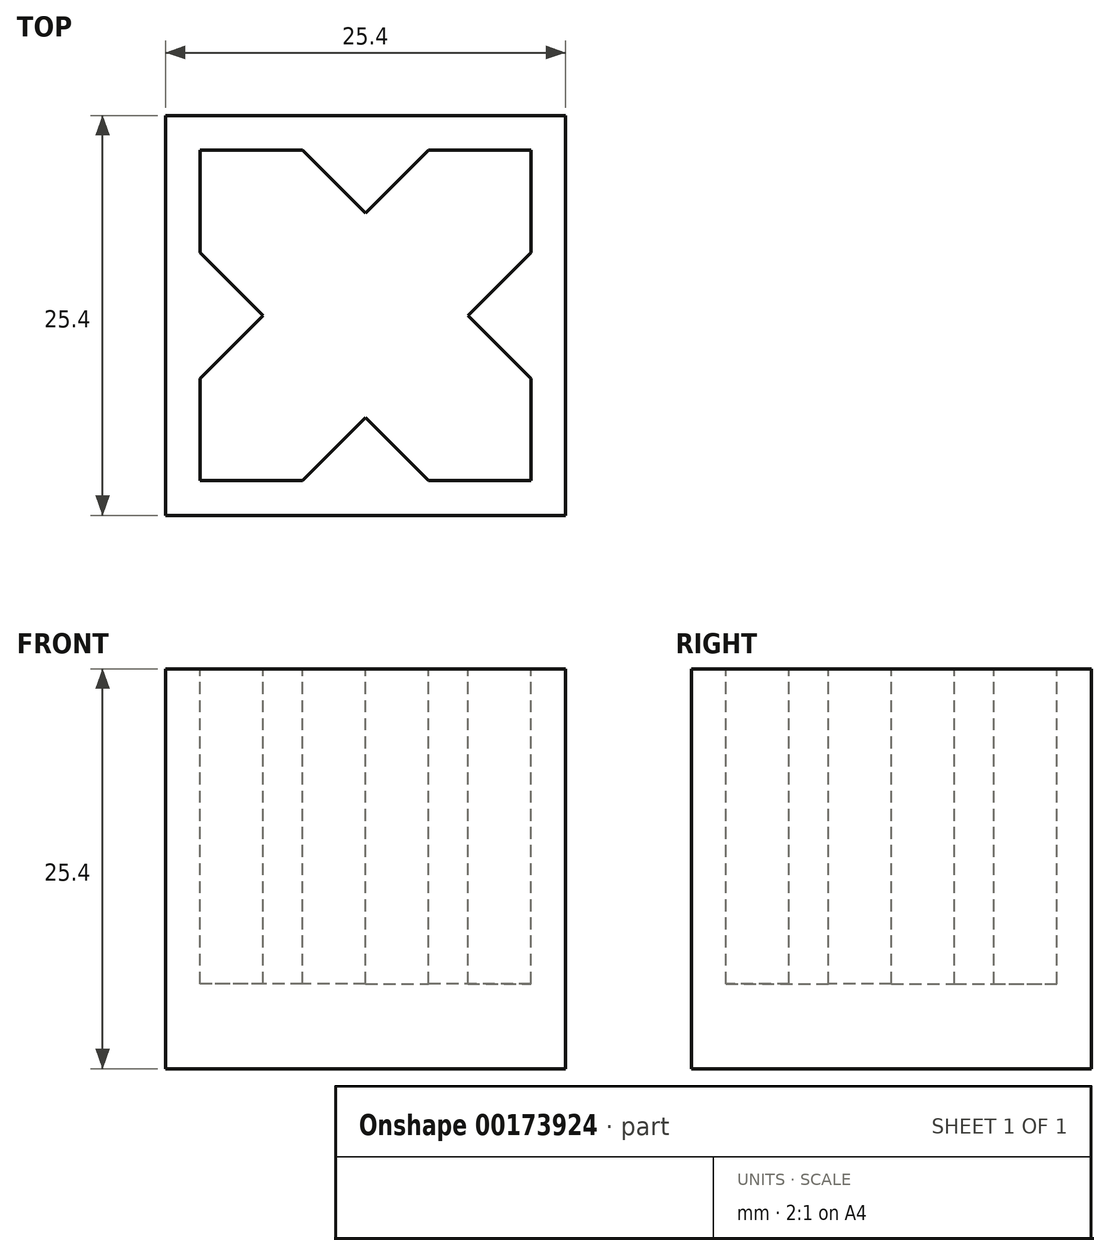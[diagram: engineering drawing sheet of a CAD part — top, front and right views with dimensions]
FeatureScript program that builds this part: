
annotation { "Feature Type Name" : "Feature", "Feature Type Description" : "" }
export const myFeature = defineFeature(function(context is Context, id is Id, definition is map)
    precondition{}
    {
        {
            var Q0;
            Q0=qCreatedBy(makeId("Top.planeOp"),FACE);
            var sketch = newSketch(context, id + "F0", { "sketchPlane" : qUnion([Q0])});
            skLineSegment(sketch, "E0.bottom", {"start": v(0, 0) * mm, "end": v(25.4, 0) * mm});
            skLineSegment(sketch, "E0.top", {"start": v(0, 25.4) * mm, "end": v(25.4, 25.4) * mm});
            skLineSegment(sketch, "E0.left", {"start": v(0, 0) * mm, "end": v(0, 25.4) * mm});
            skLineSegment(sketch, "E0.right", {"start": v(25.4, 0) * mm, "end": v(25.4, 25.4) * mm});
            skSolve(sketch);
        }
        {
            var Q0;
            Q0 = qSketchRegion(id + "F0", true);
            extrude(context, id + "F1", {"entities" : qUnion([Q0]), "depth" : 25.4 * mm});
        }
        {
            var Q0;
            Q0=makeQuery(id+"F1.opExtrude","CAP_FACE",FACE,{"disambiguationData":[OSD([sQuery(id+"F0.wireOp",EDGE,"E0.bottom"),sQuery(id+"F0.wireOp",EDGE,"E0.top"),sQuery(id+"F0.wireOp",EDGE,"E0.left"),sQuery(id+"F0.wireOp",EDGE,"E0.right")])],"isStart":false});
            var sketch = newSketch(context, id + "F2", { "sketchPlane" : qUnion([Q0])});
            skLineSegment(sketch, "E1", {"start": v(0, 12.7) * mm, "end": v(25.4, 12.7) * mm});
            skLineSegment(sketch, "E2", {"start": v(12.7, 25.4) * mm, "end": v(12.7, 0) * mm});
            skLineSegment(sketch, "E3.bottom", {"start": v(23.2, 2.2) * mm, "end": v(2.2, 2.2) * mm});
            skLineSegment(sketch, "E3.top", {"start": v(23.2, 23.2) * mm, "end": v(2.2, 23.2) * mm});
            skLineSegment(sketch, "E3.left", {"start": v(23.2, 2.2) * mm, "end": v(23.2, 23.2) * mm});
            skLineSegment(sketch, "E3.right", {"start": v(2.2, 2.2) * mm, "end": v(2.2, 23.2) * mm});
            skPoint(sketch, "E3.middle", {"position": v(12.7, 12.7) * mm});
            skLineSegment(sketch, "E4", {"start": v(12.7, 6.2) * mm, "end": v(8.7, 2.2) * mm});
            skLineSegment(sketch, "E5", {"start": v(12.7, 6.2) * mm, "end": v(16.7, 2.2) * mm});
            skLineSegment(sketch, "E6.1.0", {"start": v(19.2, 12.7) * mm, "end": v(23.2, 16.7) * mm});
            skLineSegment(sketch, "E6.1.1", {"start": v(19.2, 12.7) * mm, "end": v(23.2, 8.7) * mm});
            skLineSegment(sketch, "E6.2.0", {"start": v(12.7, 19.2) * mm, "end": v(8.7, 23.2) * mm});
            skLineSegment(sketch, "E6.2.1", {"start": v(12.7, 19.2) * mm, "end": v(16.7, 23.2) * mm});
            skLineSegment(sketch, "E6.3.0", {"start": v(6.2, 12.7) * mm, "end": v(2.2, 8.7) * mm});
            skLineSegment(sketch, "E6.3.1", {"start": v(6.2, 12.7) * mm, "end": v(2.2, 16.7) * mm});
            skSolve(sketch);
        }
        {
            var Q0;
            {var subQ4=sQuery(id+"F2.wireOp",EDGE,"E5");Q0=makeQuery(id+"F2.imprint","IMPRINT",FACE,{"disambiguationData":[TD([[makeQuery(id+"F2.imprint","IMPRINT",EDGE,{"derivedFrom":subQ4}),1.0]])]});}
            var Q1;
            {var subQ3=sQuery(id+"F2.wireOp",EDGE,"E6.1.0");Q1=makeQuery(id+"F2.imprint","IMPRINT",FACE,{"disambiguationData":[TD([[makeQuery(id+"F2.imprint","IMPRINT",EDGE,{"derivedFrom":subQ3}),1.0]])]});}
            var Q2;
            {var subQ3=sQuery(id+"F2.wireOp",EDGE,"E4");Q2=makeQuery(id+"F2.imprint","IMPRINT",FACE,{"disambiguationData":[TD([[makeQuery(id+"F2.imprint","IMPRINT",EDGE,{"derivedFrom":subQ3}),-1.0]])]});}
            var Q3;
            {var subQ4=sQuery(id+"F2.wireOp",EDGE,"E6.2.0");Q3=makeQuery(id+"F2.imprint","IMPRINT",FACE,{"disambiguationData":[TD([[makeQuery(id+"F2.imprint","IMPRINT",EDGE,{"derivedFrom":subQ4}),1.0]])]});}
            extrude(context, id + "F3", {"entities" : qUnion([Q0, Q1, Q2, Q3]), "operationType" : NewBodyOperationType.REMOVE, "oppositeDirection" : true, "depth" : 20 * mm});
        }
    });
